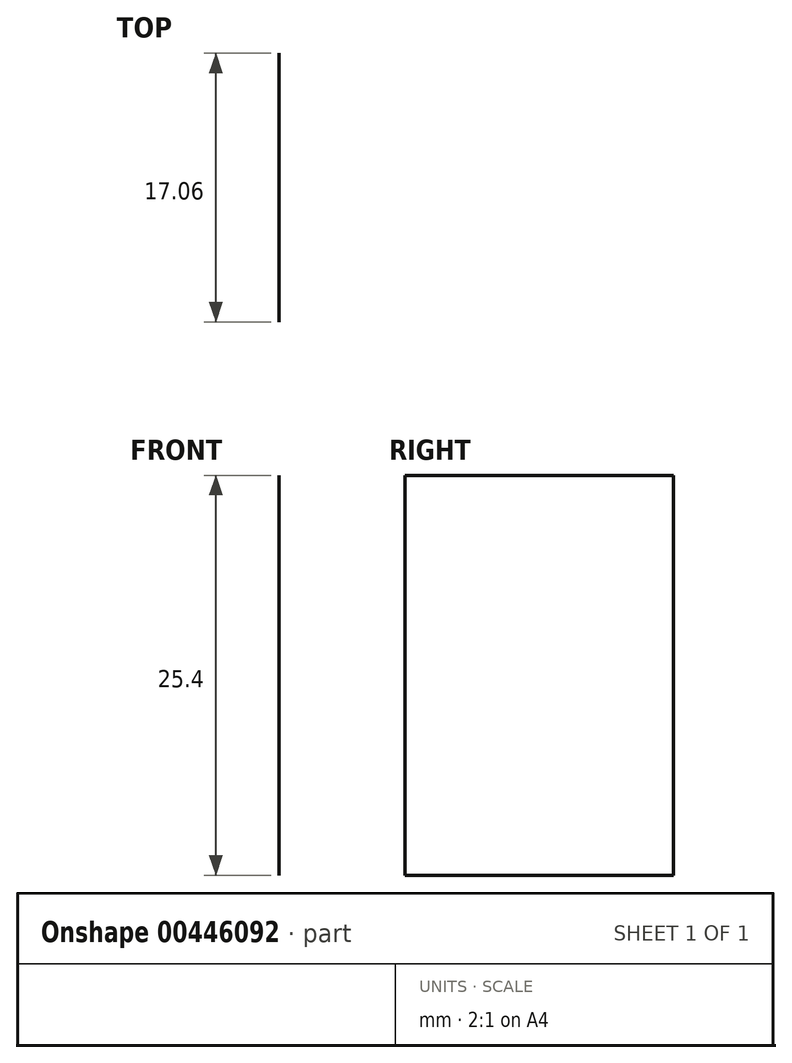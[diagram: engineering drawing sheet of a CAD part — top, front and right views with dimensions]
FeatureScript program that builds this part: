
annotation { "Feature Type Name" : "Feature", "Feature Type Description" : "" }
export const myFeature = defineFeature(function(context is Context, id is Id, definition is map)
    precondition{}
    {
        {
            var Q0;
            Q0=qCreatedBy(makeId("Top.planeOp"),FACE);
            var sketch = newSketch(context, id + "F0", { "sketchPlane" : qUnion([Q0])});
            skCircle(sketch, "E0", {"center": v(0, 0) * mm, "radius": 45.72 * mm});
            skCircle(sketch, "E1", {"center": v(0, 0) * mm, "radius": 30.48 * mm});
            skLineSegment(sketch, "E2", {"start": v(0, 0) * mm, "end": v(30.48, 0) * mm, "construction": true});
            skLineSegment(sketch, "E3", {"start": v(0, 0) * mm, "end": v(0, -45.72) * mm, "construction": true});
            skLineSegment(sketch, "E4.bottom", {"start": v(-29.26, 8.53) * mm, "end": v(-16.43, 8.53) * mm});
            skLineSegment(sketch, "E4.top", {"start": v(-29.26, -8.53) * mm, "end": v(-16.43, -8.53) * mm});
            skLineSegment(sketch, "E4.left", {"start": v(-29.26, 8.53) * mm, "end": v(-29.26, -8.53) * mm});
            skLineSegment(sketch, "E4.right", {"start": v(-16.43, 8.53) * mm, "end": v(-16.43, -8.53) * mm});
            skLineSegment(sketch, "E5", {"start": v(-16.43, 0) * mm, "end": v(0, 0) * mm, "construction": true});
            skSolve(sketch);
        }
        {
            var Q0;
            Q0=makeQuery(id+"F0.imprint","IMPRINT",FACE,{"disambiguationData":[TD([[makeQuery(id+"F0.imprint","IMPRINT",EDGE,{"derivedFrom":sQuery(id+"F0.wireOp",EDGE,"E4.bottom")}),-1.0]])]});
            var Q1;
            Q1=sQuery(id+"F0.wireOp",EDGE,"E4.left");
            extrude(context, id + "F1", {"entities" : qUnion([Q0]), "bodyType" : ToolBodyType.SURFACE, "surfaceEntities" : qUnion([Q1]), "depth" : 25.4 * mm});
        }
    });
